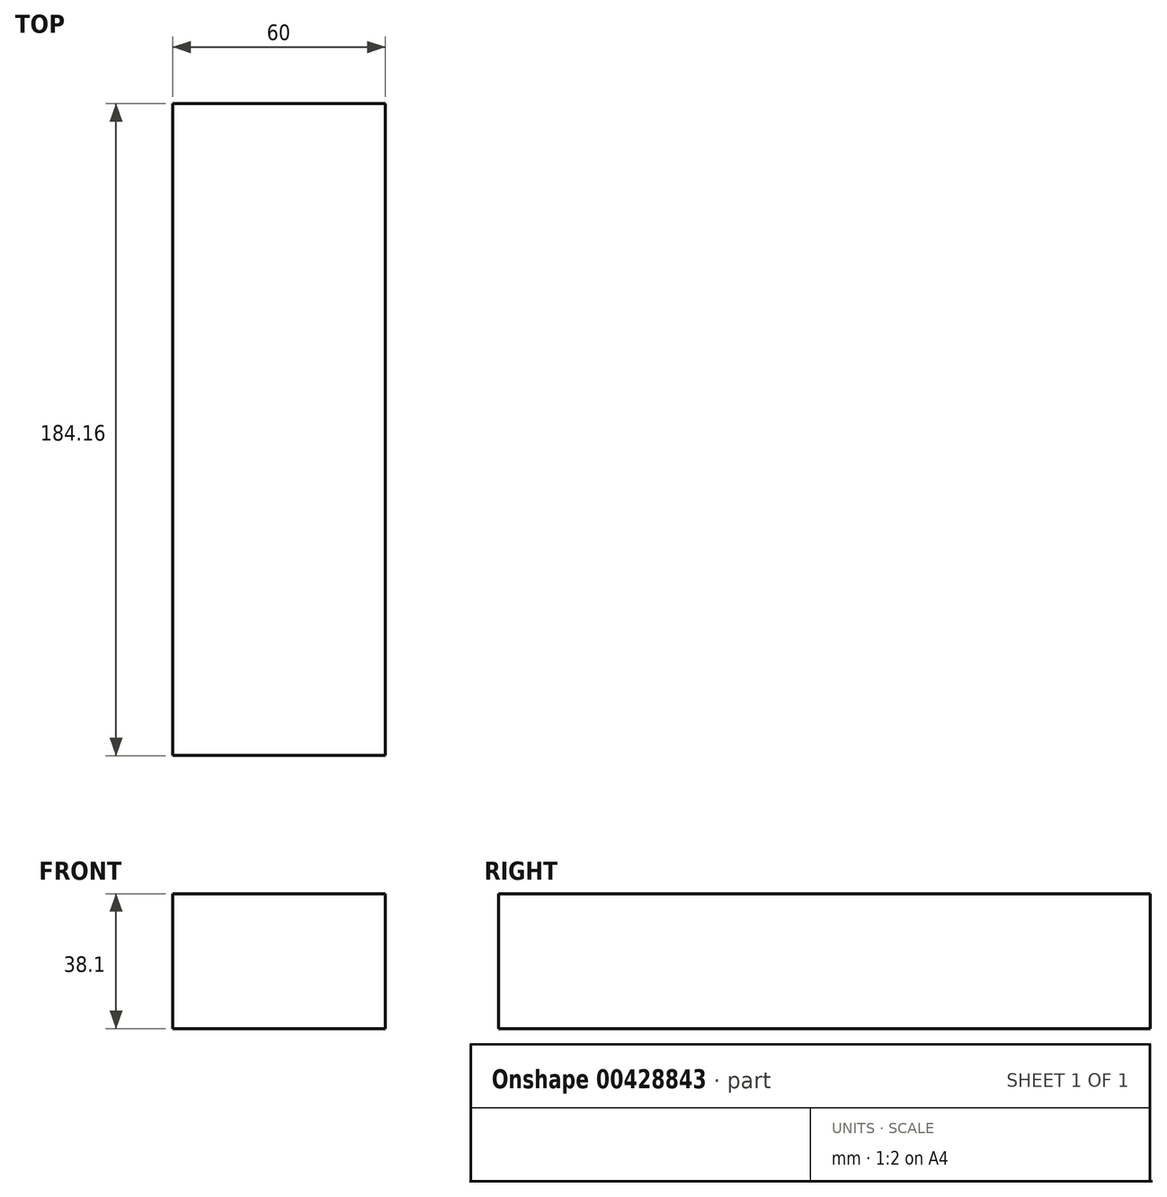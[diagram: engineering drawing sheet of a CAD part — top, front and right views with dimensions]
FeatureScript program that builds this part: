
annotation { "Feature Type Name" : "Feature", "Feature Type Description" : "" }
export const myFeature = defineFeature(function(context is Context, id is Id, definition is map)
    precondition{}
    {
        {
            assignVariable(context, id + "F0", {"name" : "Length", "anyValue" : 60});
        }
        {
            var Q0;
            Q0=qCreatedBy(makeId("Right.planeOp"),FACE);
            var sketch = newSketch(context, id + "F1", { "sketchPlane" : qUnion([Q0])});
            skLineSegment(sketch, "E0.bottom", {"start": v(92.08, -19.05) * mm, "end": v(-92.08, -19.05) * mm});
            skLineSegment(sketch, "E0.top", {"start": v(92.08, 19.05) * mm, "end": v(-92.08, 19.05) * mm});
            skLineSegment(sketch, "E0.left", {"start": v(92.08, -19.05) * mm, "end": v(92.08, 19.05) * mm});
            skLineSegment(sketch, "E0.right", {"start": v(-92.08, -19.05) * mm, "end": v(-92.08, 19.05) * mm});
            skPoint(sketch, "E0.middle", {"position": v(0, 0) * mm});
            skSolve(sketch);
        }
        {
            var Q0;
            Q0 = qSketchRegion(id + "F1", true);
            extrude(context, id + "F2", {"entities" : qUnion([Q0]), "depth" : (getVariable(context, 'Length')) * mm, "symmetric" : true});
        }
    });
